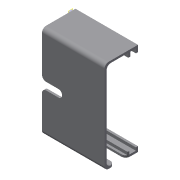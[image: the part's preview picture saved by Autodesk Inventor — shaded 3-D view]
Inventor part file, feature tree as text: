
AUTODESK INVENTOR PART (.ipt)
format: ipt  version: 2019.4 (Build 234330000, 330)  size: 164,864 bytes
history: native  units: mm
features: other x4, sketch x3, extrude x3, plane x2, fillet x2, reference x2, projected_geometry x1
ambient origin geometry x8: Origin, YZ Plane, XZ Plane, XY Plane, X Axis, Y Axis, Z Axis, Center Point
bodies: Solid1 (feature_tree)
feature tree (17):
  plane  "Work Plane1"
  sketch  "Sketch1"  dims[d0=1.0mm d1=1.0mm d2=3.0mm]
  plane  "Work Plane2"
  extrude  "Extrusion1"  Depth=3.0mm
  fillet  "Fillet1"  Radius=3.0mm
  extrude  "Extrusion2"  Depth=3.0mm
  extrude  "Extrusion3"  Depth=3.0mm
  fillet  "Fillet2"  Radius=3.0mm
  reference  "Reference1"
  sketch  "Sketch2"  dims[d3=3.0mm d4=35.0mm]
  reference  "Reference2"
  sketch  "Sketch3"  dims[d5=3.0mm d6=3.0mm d7=3.0mm d8=3.0mm d10=1.0mm d11=1.0mm d12=1.0mm d13=10.0mm d14=0.0mm d15=6.0mm d16=10.0mm d17=0.0mm d18=10.0mm d19=0.0mm d20=6.0mm]
  projected_geometry  "Projected Loop1"
  other  "Assembly_Opentrons_Imagingunit_v3.iam"
  other  "04_OPENTRONS_Microscope_wellplate_base:1"
  other  "Assembly_opentrons_microscope_slide_y_base:1"
  other  "02_Opentrons_Microscope_Base_v0:1"
